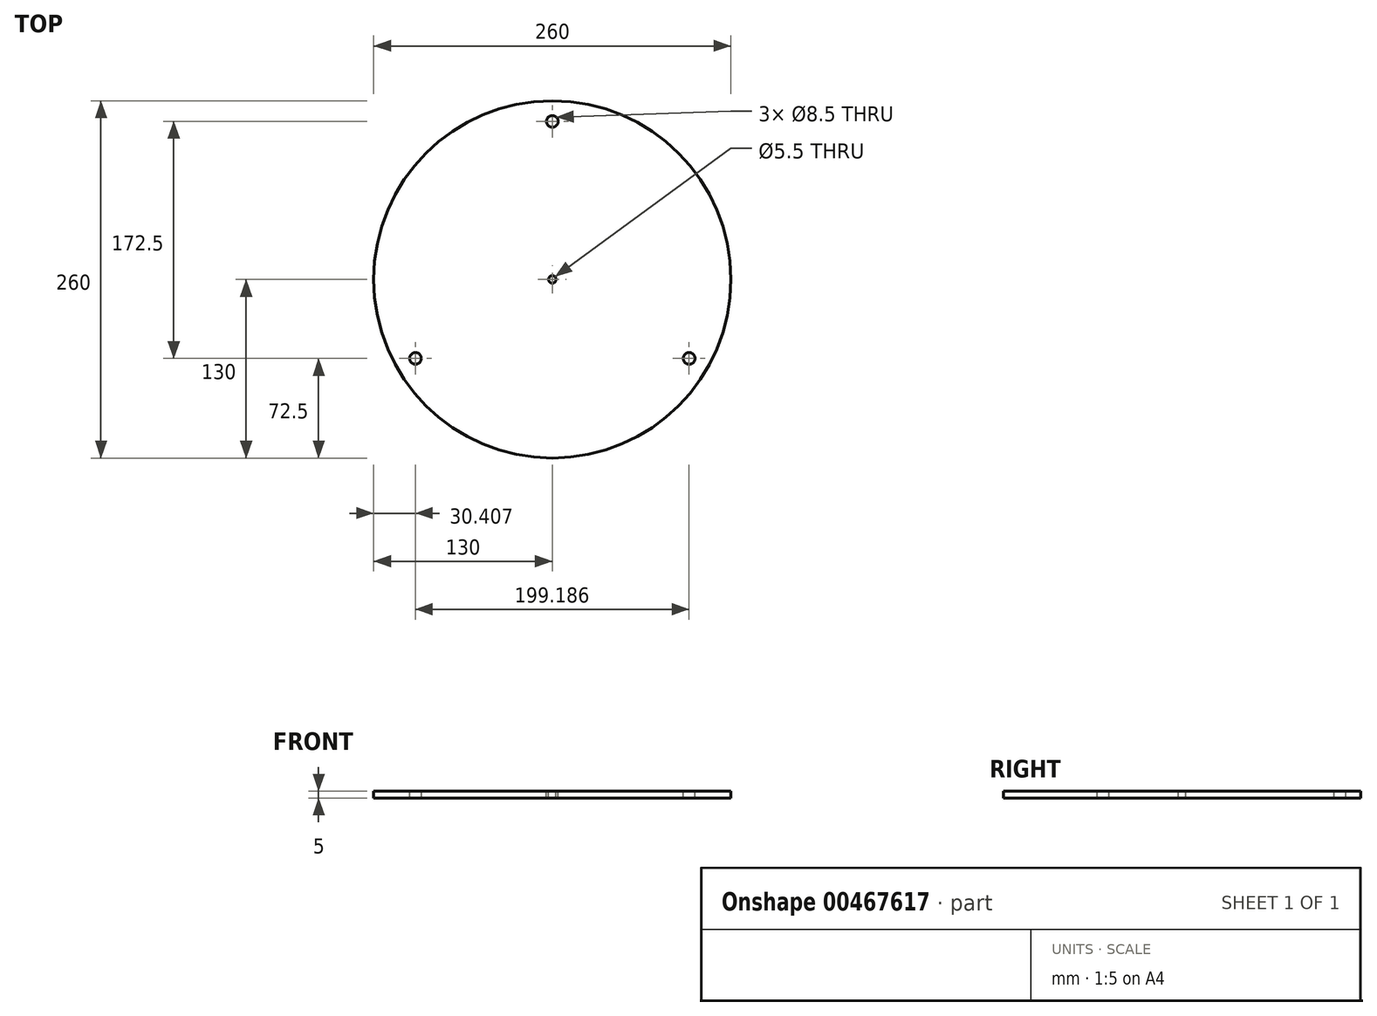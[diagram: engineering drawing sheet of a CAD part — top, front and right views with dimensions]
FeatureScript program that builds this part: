
annotation { "Feature Type Name" : "Feature", "Feature Type Description" : "" }
export const myFeature = defineFeature(function(context is Context, id is Id, definition is map)
    precondition{}
    {
        {
            var Q0;
            Q0=qCreatedBy(makeId("Top.planeOp"),FACE);
            var sketch = newSketch(context, id + "F0", { "sketchPlane" : qUnion([Q0])});
            skCircle(sketch, "E0", {"center": v(0, 0) * mm, "radius": 130 * mm});
            skSolve(sketch);
        }
        {
            var Q0;
            Q0=makeQuery(id+"F0.imprint","IMPRINT",FACE,{"disambiguationData":[TD([[makeQuery(id+"F0.imprint","IMPRINT",EDGE,{"derivedFrom":sQuery(id+"F0.wireOp",EDGE,"E0")}),1.0]])]});
            extrude(context, id + "F1", {"entities" : qUnion([Q0]), "depth" : 5 * mm});
        }
        {
            var Q0;
            Q0=makeQuery(id+"F1.opExtrude","CAP_FACE",FACE,{"disambiguationData":[OSD([sQuery(id+"F0.wireOp",EDGE,"E0")])],"isStart":false});
            var sketch = newSketch(context, id + "F2", { "sketchPlane" : qUnion([Q0])});
            skCircle(sketch, "E1", {"center": v(0, 0) * mm, "radius": 2.75 * mm});
            skCircle(sketch, "E2", {"center": v(0, 0) * mm, "radius": 115 * mm, "construction": true});
            skCircle(sketch, "E3", {"center": v(0, 115) * mm, "radius": 4.25 * mm});
            skLineSegment(sketch, "E4", {"start": v(0, 0) * mm, "end": v(-124.93, -72.13) * mm, "construction": true});
            skLineSegment(sketch, "E5", {"start": v(0, 0) * mm, "end": v(118.24, -68.27) * mm, "construction": true});
            skCircle(sketch, "E6", {"center": v(-99.6, -57.5) * mm, "radius": 4.25 * mm});
            skCircle(sketch, "E7", {"center": v(99.6, -57.5) * mm, "radius": 4.25 * mm});
            skSolve(sketch);
        }
        {
            var Q0;
            Q0 = qSketchRegion(id + "F2", true);
            extrude(context, id + "F3", {"entities" : qUnion([Q0]), "operationType" : NewBodyOperationType.REMOVE, "endBound" : BoundingType.THROUGH_ALL, "oppositeDirection" : true, "depth" : 25 * mm});
        }
    });
